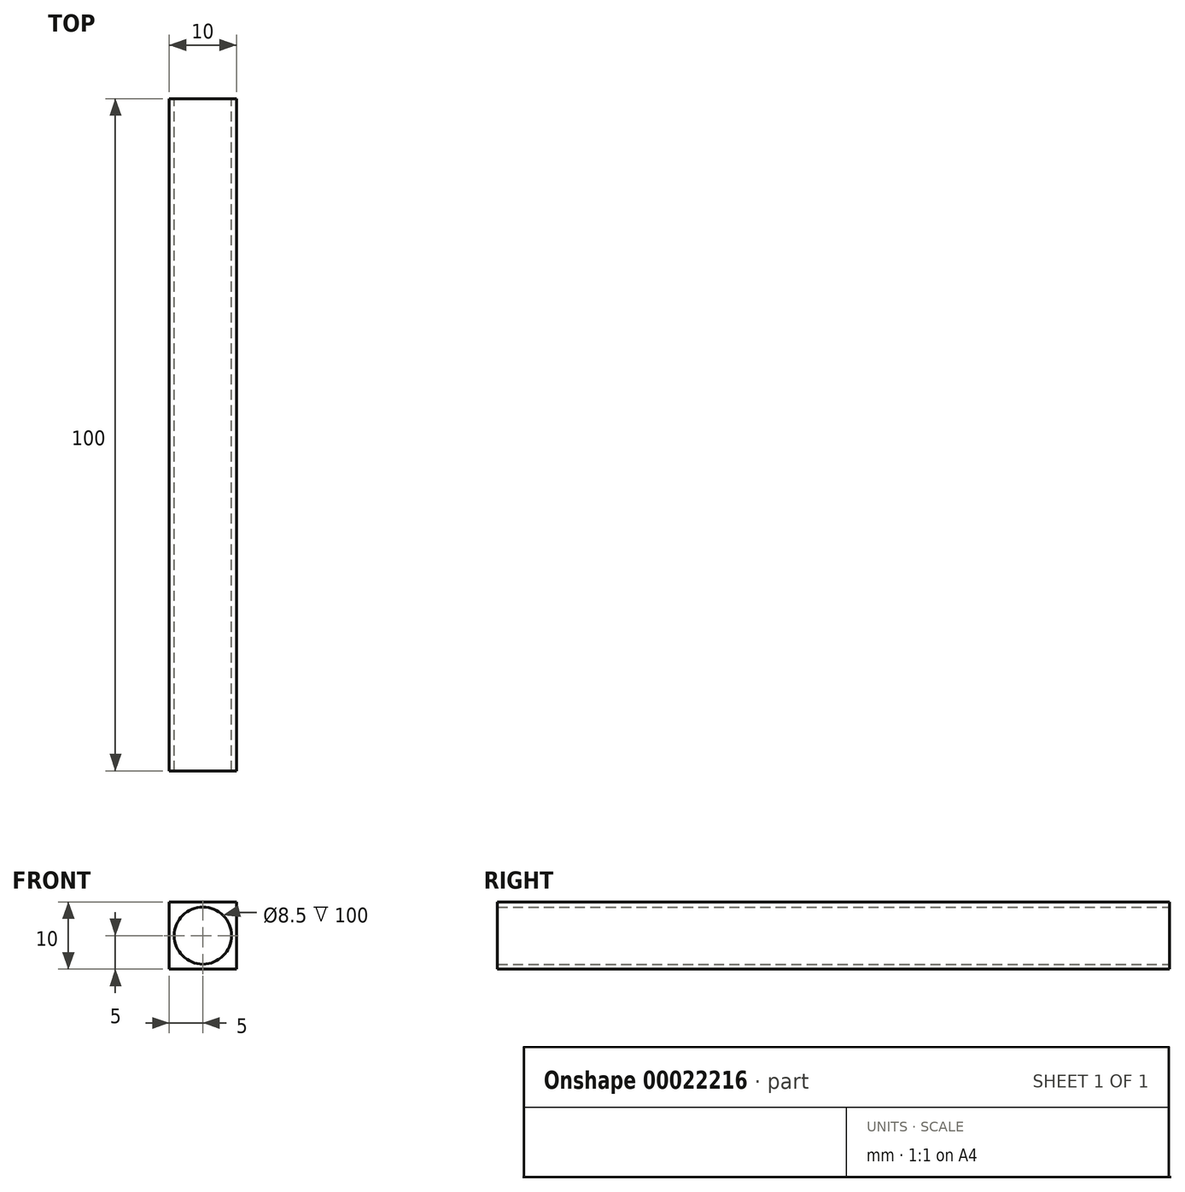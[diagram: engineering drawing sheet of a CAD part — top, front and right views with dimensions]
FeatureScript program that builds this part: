
annotation { "Feature Type Name" : "Feature", "Feature Type Description" : "" }
export const myFeature = defineFeature(function(context is Context, id is Id, definition is map)
    precondition{}
    {
        {
            var Q0;
            Q0=qCreatedBy(makeId("Front.planeOp"),FACE);
            var sketch = newSketch(context, id + "F0", { "sketchPlane" : qUnion([Q0])});
            skCircle(sketch, "E0", {"center": v(0, 0) * mm, "radius": 4.25 * mm});
            skLineSegment(sketch, "E1.rect.bottom", {"start": v(4.5, -5) * mm, "end": v(-4.5, -5) * mm});
            skLineSegment(sketch, "E1.rect.top", {"start": v(4.5, 5) * mm, "end": v(-4.5, 5) * mm});
            skLineSegment(sketch, "E1.rect.left", {"start": v(5, -4.5) * mm, "end": v(5, 4.5) * mm});
            skLineSegment(sketch, "E1.rect.right", {"start": v(-5, -4.5) * mm, "end": v(-5, 4.5) * mm});
            skPoint(sketch, "E2.visualSharp", {"position": v(-5, 5) * mm});
            skPoint(sketch, "E3.visualSharp", {"position": v(5, 5) * mm});
            skPoint(sketch, "E4.visualSharp", {"position": v(5, -5) * mm});
            skPoint(sketch, "E5.visualSharp", {"position": v(-5, -5) * mm});
            skLineSegment(sketch, "E6", {"start": v(-5, 4.5) * mm, "end": v(-5, 5) * mm});
            skLineSegment(sketch, "E7", {"start": v(-4.5, 5) * mm, "end": v(-5, 5) * mm});
            skLineSegment(sketch, "E8", {"start": v(4.5, 5) * mm, "end": v(5, 5) * mm});
            skLineSegment(sketch, "E9", {"start": v(5, 4.5) * mm, "end": v(5, 5) * mm});
            skLineSegment(sketch, "E10", {"start": v(4.5, -5) * mm, "end": v(5, -5) * mm});
            skLineSegment(sketch, "E11", {"start": v(5, -4.5) * mm, "end": v(5, -5) * mm});
            skLineSegment(sketch, "E12", {"start": v(-5, -4.5) * mm, "end": v(-5, -5) * mm});
            skLineSegment(sketch, "E13", {"start": v(-4.5, -5) * mm, "end": v(-5, -5) * mm});
            skSolve(sketch);
        }
        {
            var Q0;
            Q0=makeQuery(id+"F0.imprint","IMPRINT",FACE,{"disambiguationData":[TD([[makeQuery(id+"F0.imprint","IMPRINT",EDGE,{"derivedFrom":sQuery(id+"F0.wireOp",EDGE,"E0")}),-1.0]])]});
            extrude(context, id + "F1", {"entities" : qUnion([Q0]), "depth" : 100 * mm});
        }
    });
